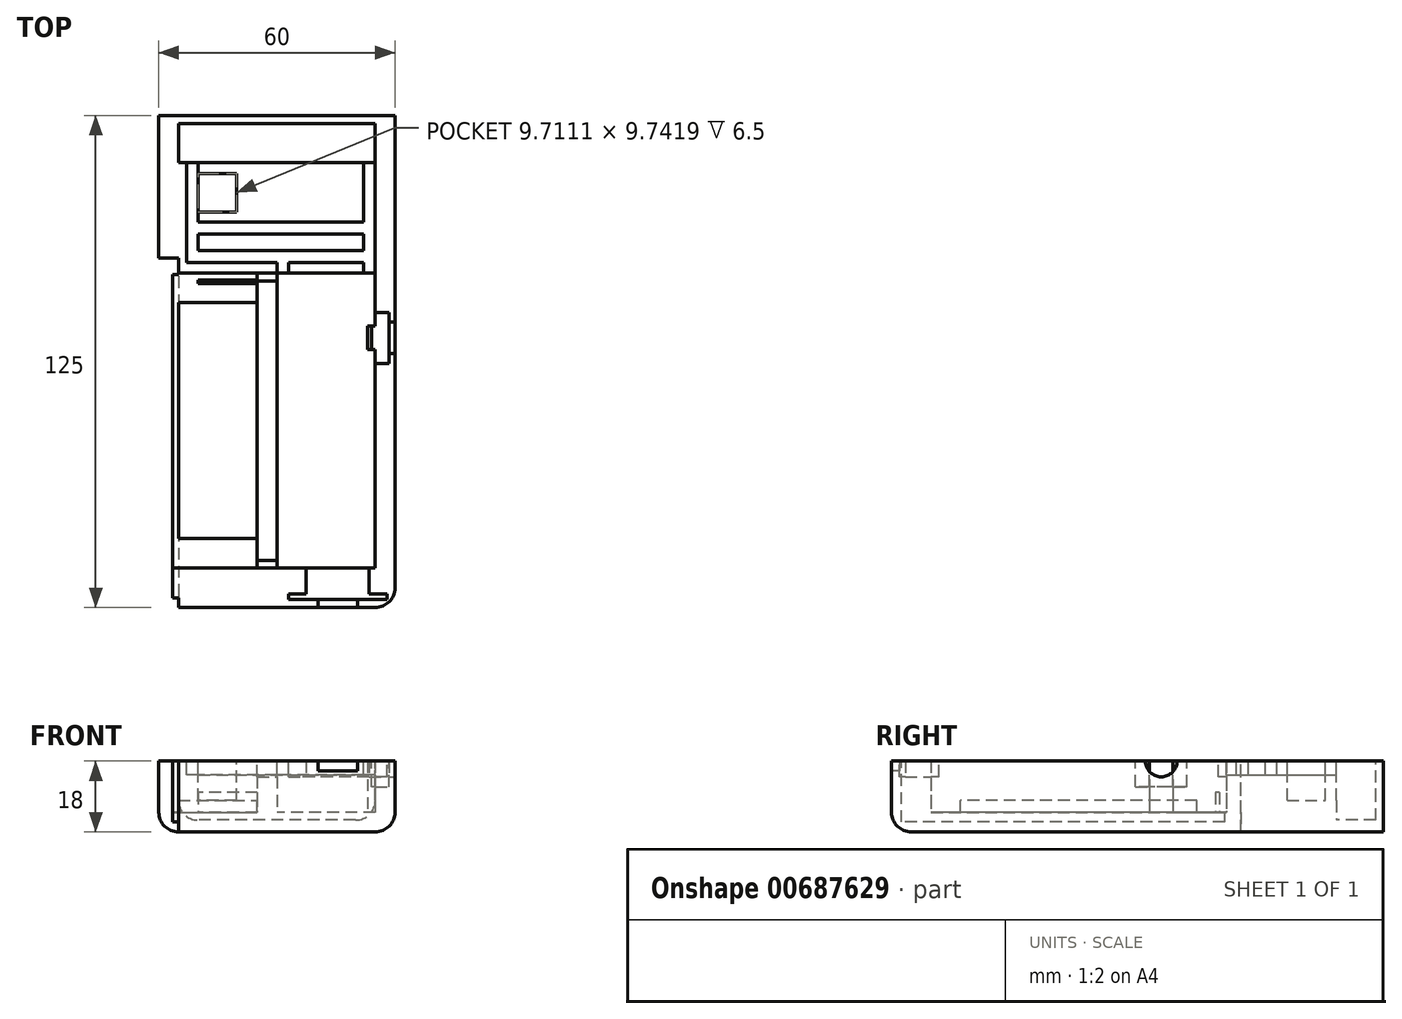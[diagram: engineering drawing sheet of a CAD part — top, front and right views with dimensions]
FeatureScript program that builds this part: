
annotation { "Feature Type Name" : "Feature", "Feature Type Description" : "" }
export const myFeature = defineFeature(function(context is Context, id is Id, definition is map)
    precondition{}
    {
        {
            var Q0;
            Q0=qCreatedBy(makeId("Top.planeOp"),FACE);
            var sketch = newSketch(context, id + "F0", { "sketchPlane" : qUnion([Q0])});
            skLineSegment(sketch, "E0.bottom", {"start": v(-46.34, 47.02) * mm, "end": v(13.66, 47.02) * mm});
            skLineSegment(sketch, "E0.top", {"start": v(-46.34, -52.98) * mm, "end": v(13.66, -52.98) * mm});
            skLineSegment(sketch, "E0.left", {"start": v(-46.34, 47.02) * mm, "end": v(-46.34, -52.98) * mm});
            skLineSegment(sketch, "E0.right", {"start": v(13.66, 47.02) * mm, "end": v(13.66, -52.98) * mm});
            skLineSegment(sketch, "E1.bottom", {"start": v(8.66, -42.98) * mm, "end": v(-16.34, -42.98) * mm});
            skLineSegment(sketch, "E1.top", {"start": v(8.66, 32.02) * mm, "end": v(-16.34, 32.02) * mm});
            skLineSegment(sketch, "E1.left", {"start": v(8.66, -42.98) * mm, "end": v(8.66, 32.02) * mm});
            skLineSegment(sketch, "E1.right", {"start": v(-16.34, -42.98) * mm, "end": v(-16.34, 32.02) * mm});
            skLineSegment(sketch, "E2.bottom", {"start": v(-41.34, 32.02) * mm, "end": v(-21.34, 32.02) * mm});
            skLineSegment(sketch, "E2.top", {"start": v(-41.34, -42.98) * mm, "end": v(-21.34, -42.98) * mm});
            skLineSegment(sketch, "E2.left", {"start": v(-41.34, 32.02) * mm, "end": v(-41.34, -42.98) * mm});
            skLineSegment(sketch, "E2.right", {"start": v(-21.34, 32.02) * mm, "end": v(-21.34, -42.98) * mm});
            skLineSegment(sketch, "E3.bottom", {"start": v(-46.34, 47.02) * mm, "end": v(-26.34, 47.02) * mm});
            skLineSegment(sketch, "E4.bottom", {"start": v(13.66, 47.02) * mm, "end": v(-6.34, 47.02) * mm});
            skSolve(sketch);
        }
        {
            var Q0;
            Q0=makeQuery(id+"F0.imprint","IMPRINT",FACE,{"disambiguationData":[TD([[makeQuery(id+"F0.imprint","IMPRINT",EDGE,{"derivedFrom":sQuery(id+"F0.wireOp",EDGE,"E0.bottom")}),-1.0]])]});
            extrude(context, id + "F1", {"entities" : qUnion([Q0]), "depth" : 13 * mm, "offsetDistance" : 25 * mm});
        }
        {
            var Q0;
            Q0=makeQuery(id+"F0.imprint","IMPRINT",FACE,{"disambiguationData":[TD([[makeQuery(id+"F0.imprint","IMPRINT",EDGE,{"derivedFrom":sQuery(id+"F0.wireOp",EDGE,"E1.bottom")}),-1.0]])]});
            var Q1;
            Q1=makeQuery(id+"F0.imprint","IMPRINT",FACE,{"disambiguationData":[TD([[makeQuery(id+"F0.imprint","IMPRINT",EDGE,{"derivedFrom":sQuery(id+"F0.wireOp",EDGE,"E2.bottom")}),-1.0]])]});
            var Q2;
            Q2=makeQuery(id+"F0.imprint","IMPRINT",FACE,{"disambiguationData":[TD([[makeQuery(id+"F0.imprint","IMPRINT",EDGE,{"derivedFrom":sQuery(id+"F0.wireOp",EDGE,"E0.bottom")}),-1.0]])]});
            extrude(context, id + "F2", {"entities" : qUnion([Q0, Q1, Q2]), "operationType" : NewBodyOperationType.ADD, "oppositeDirection" : true, "depth" : 5 * mm, "offsetDistance" : 25 * mm});
        }
        {
            var Q0;
            {var subQ0=sQuery(id+"F0.wireOp",EDGE,"E0.right");Q0=makeQuery(id+"F2.boolean.opBoolean","MERGE",FACE,{"derivedFrom":[makeQuery(id+"F1.opExtrude","SWEPT_FACE",FACE,{"disambiguationData":[OSD([subQ0])]}),makeQuery(id+"F2.opExtrude","SWEPT_FACE",FACE,{"disambiguationData":[OSD([subQ0])]})]});}
            var sketch = newSketch(context, id + "F3", { "sketchPlane" : qUnion([Q0])});
            skCircle(sketch, "E5", {"center": v(15.53, 13) * mm, "radius": 4 * mm});
            skSolve(sketch);
        }
        {
            var Q0;
            Q0 = qSketchRegion(id + "F3", true);
            extrude(context, id + "F4", {"entities" : qUnion([Q0]), "operationType" : NewBodyOperationType.REMOVE, "oppositeDirection" : true, "depth" : 5 * mm, "offsetDistance" : 25 * mm});
        }
        {
            var Q0;
            {var subQ0=sQuery(id+"F0.wireOp",EDGE,"E4.bottom");var subQ1=sQuery(id+"F0.wireOp",EDGE,"E3.bottom");Q0=makeQuery(id+"FooMiOLfBCFiUER_0.boolean.opBoolean","MERGE",FACE,{"derivedFrom":[makeQuery(id+"F1.opExtrude","CAP_FACE",FACE,{"disambiguationData":[OSD([sQuery(id+"F0.wireOp",EDGE,"E0.bottom"),sQuery(id+"F0.wireOp",EDGE,"E0.top"),sQuery(id+"F0.wireOp",EDGE,"E0.left"),sQuery(id+"F0.wireOp",EDGE,"E0.right"),sQuery(id+"F0.wireOp",EDGE,"E1.bottom"),sQuery(id+"F0.wireOp",EDGE,"E1.top"),sQuery(id+"F0.wireOp",EDGE,"E1.left"),sQuery(id+"F0.wireOp",EDGE,"E1.right"),sQuery(id+"F0.wireOp",EDGE,"E2.bottom"),sQuery(id+"F0.wireOp",EDGE,"E2.top"),sQuery(id+"F0.wireOp",EDGE,"E2.left"),sQuery(id+"F0.wireOp",EDGE,"E2.right"),subQ1,subQ0])],"isStart":false}),makeQuery(id+"FooMiOLfBCFiUER_0.opExtrude","CAP_FACE",FACE,{"disambiguationData":[OSD([subQ1,sQuery(id+"F0.wireOp",EDGE,"E3.top"),sQuery(id+"F0.wireOp",EDGE,"E3.right"),sQuery(id+"F0.wireOp",EDGE,"7eb4718d-a1aa-4163-babb-219306aed6bf")])],"isStart":false}),makeQuery(id+"FooMiOLfBCFiUER_0.opExtrude","CAP_FACE",FACE,{"disambiguationData":[OSD([subQ0,sQuery(id+"F0.wireOp",EDGE,"E4.top"),sQuery(id+"F0.wireOp",EDGE,"E4.right"),sQuery(id+"F0.wireOp",EDGE,"1b457c1d-76ec-41e5-a347-412c3d054c09")])],"isStart":false})]});}
            var sketch = newSketch(context, id + "F5", { "sketchPlane" : qUnion([Q0])});
            skLineSegment(sketch, "E6.bottom", {"start": v(8.66, 22.03) * mm, "end": v(12.16, 22.03) * mm});
            skLineSegment(sketch, "E6.top", {"start": v(8.66, 9.03) * mm, "end": v(12.16, 9.03) * mm});
            skLineSegment(sketch, "E6.left", {"start": v(8.66, 22.03) * mm, "end": v(8.66, 9.03) * mm});
            skLineSegment(sketch, "E6.right", {"start": v(12.16, 22.03) * mm, "end": v(12.16, 9.03) * mm});
            skSolve(sketch);
        }
        {
            var Q0;
            Q0 = qSketchRegion(id + "F5", true);
            extrude(context, id + "F6", {"entities" : qUnion([Q0]), "operationType" : NewBodyOperationType.REMOVE, "oppositeDirection" : true, "depth" : 6.5 * mm, "offsetDistance" : 25 * mm});
        }
        {
            var Q0;
            {var subQ0=sQuery(id+"F0.wireOp",EDGE,"E0.left");Q0=makeQuery(id+"F2.boolean.opBoolean","MERGE",FACE,{"derivedFrom":[makeQuery(id+"F1.opExtrude","SWEPT_FACE",FACE,{"disambiguationData":[OSD([subQ0])]}),makeQuery(id+"F2.opExtrude","SWEPT_FACE",FACE,{"disambiguationData":[OSD([subQ0])]})]});}
            var sketch = newSketch(context, id + "F7", { "sketchPlane" : qUnion([Q0])});
            skLineSegment(sketch, "E7.bottom", {"start": v(-35.8, -5) * mm, "end": v(52.98, -5) * mm});
            skLineSegment(sketch, "E7.top", {"start": v(-35.8, 13) * mm, "end": v(52.98, 13) * mm});
            skLineSegment(sketch, "E7.left", {"start": v(-35.8, -5) * mm, "end": v(-35.8, 13) * mm});
            skLineSegment(sketch, "E7.right", {"start": v(52.98, -5) * mm, "end": v(52.98, 13) * mm});
            skSolve(sketch);
        }
        {
            var Q0;
            Q0 = qSketchRegion(id + "F7", true);
            extrude(context, id + "F8", {"entities" : qUnion([Q0]), "operationType" : NewBodyOperationType.REMOVE, "oppositeDirection" : true, "depth" : 5 * mm, "offsetDistance" : 25 * mm});
        }
        {
            var Q0;
            Q0=makeQuery(id+"F8.boolean.opBoolean","COPY",FACE,{"derivedFrom":makeQuery(id+"F8.opExtrude","CAP_FACE",FACE,{"disambiguationData":[OSD([sQuery(id+"F7.wireOp",EDGE,"E7.bottom"),sQuery(id+"F7.wireOp",EDGE,"E7.top"),sQuery(id+"F7.wireOp",EDGE,"E7.left"),sQuery(id+"F7.wireOp",EDGE,"E7.right")])],"isStart":false})});
            var sketch = newSketch(context, id + "F9", { "sketchPlane" : qUnion([Q0])});
            skLineSegment(sketch, "E8.bottom", {"start": v(-33.3, -2.5) * mm, "end": v(50.48, -2.5) * mm});
            skLineSegment(sketch, "E8.top", {"start": v(-33.3, 13) * mm, "end": v(50.48, 13) * mm});
            skLineSegment(sketch, "E8.left", {"start": v(-33.3, -2.5) * mm, "end": v(-33.3, 13) * mm});
            skLineSegment(sketch, "E8.right", {"start": v(50.48, -2.5) * mm, "end": v(50.48, 13) * mm});
            skSolve(sketch);
        }
        {
            var Q0;
            Q0=makeQuery(id+"F9.imprint","IMPRINT",FACE,{"disambiguationData":[TD([[makeQuery(id+"F9.imprint","IMPRINT",EDGE,{"derivedFrom":sQuery(id+"F9.wireOp",EDGE,"E8.bottom")}),1.0]])]});
            extrude(context, id + "F10", {"entities" : qUnion([Q0]), "operationType" : NewBodyOperationType.ADD, "depth" : 5 * mm, "offsetDistance" : 25 * mm});
        }
        {
            var Q0;
            Q0=makeQuery(id+"F10.opExtrude","CAP_FACE",FACE,{"disambiguationData":[OSD([sQuery(id+"F0.wireOp",EDGE,"E2.bottom"),sQuery(id+"F0.wireOp",EDGE,"E2.top"),sQuery(id+"F0.wireOp",EDGE,"E2.left"),sQuery(id+"F9.wireOp",EDGE,"E8.bottom"),sQuery(id+"F9.wireOp",EDGE,"E8.top"),sQuery(id+"F9.wireOp",EDGE,"E8.left"),sQuery(id+"F9.wireOp",EDGE,"E8.right")])],"isStart":false});
            var sketch = newSketch(context, id + "F11", { "sketchPlane" : qUnion([Q0])});
            skLineSegment(sketch, "E9.bottom", {"start": v(-33.3, 13) * mm, "end": v(-32.02, 13) * mm});
            skLineSegment(sketch, "E9.top", {"start": v(-33.3, 0) * mm, "end": v(-32.02, 0) * mm});
            skLineSegment(sketch, "E9.left", {"start": v(-33.3, 13) * mm, "end": v(-33.3, 0) * mm});
            skLineSegment(sketch, "E9.right", {"start": v(-32.02, 13) * mm, "end": v(-32.02, 0) * mm});
            skSolve(sketch);
        }
        {
            var Q0;
            Q0 = qSketchRegion(id + "F11", true);
            extrude(context, id + "F12", {"entities" : qUnion([Q0]), "operationType" : NewBodyOperationType.REMOVE, "oppositeDirection" : true, "depth" : 5 * mm, "offsetDistance" : 25 * mm});
        }
        {
            var Q0;
            {var subQ0=sQuery(id+"F9.wireOp",EDGE,"E8.top");var subQ1=sQuery(id+"F0.wireOp",EDGE,"E2.left");var subQ2=sQuery(id+"F0.wireOp",EDGE,"E2.top");var subQ3=sQuery(id+"F0.wireOp",EDGE,"E0.top");var subQ4=sQuery(id+"F0.wireOp",EDGE,"E3.bottom");var subQ5=makeQuery(id+"FooMiOLfBCFiUER_0.opExtrude","CAP_FACE",FACE,{"disambiguationData":[OSD([subQ4,sQuery(id+"F0.wireOp",EDGE,"E3.top"),sQuery(id+"F0.wireOp",EDGE,"E3.right"),sQuery(id+"F0.wireOp",EDGE,"7eb4718d-a1aa-4163-babb-219306aed6bf")])],"isStart":false});var subQ6=sQuery(id+"F0.wireOp",EDGE,"E4.bottom");var subQ7=sQuery(id+"F0.wireOp",EDGE,"E2.bottom");var subQ8=makeQuery(id+"F1.opExtrude","CAP_FACE",FACE,{"disambiguationData":[OSD([sQuery(id+"F0.wireOp",EDGE,"E0.bottom"),subQ3,sQuery(id+"F0.wireOp",EDGE,"E0.left"),sQuery(id+"F0.wireOp",EDGE,"E0.right"),sQuery(id+"F0.wireOp",EDGE,"E1.bottom"),sQuery(id+"F0.wireOp",EDGE,"E1.top"),sQuery(id+"F0.wireOp",EDGE,"E1.left"),sQuery(id+"F0.wireOp",EDGE,"E1.right"),subQ7,subQ2,subQ1,sQuery(id+"F0.wireOp",EDGE,"E2.right"),subQ4,subQ6])],"isStart":false});var subQ12=makeQuery(id+"FooMiOLfBCFiUER_0.opExtrude","CAP_FACE",FACE,{"disambiguationData":[OSD([subQ6,sQuery(id+"F0.wireOp",EDGE,"E4.top"),sQuery(id+"F0.wireOp",EDGE,"E4.right"),sQuery(id+"F0.wireOp",EDGE,"1b457c1d-76ec-41e5-a347-412c3d054c09")])],"isStart":false});Q0=makeQuery(id+"F10.boolean.opBoolean","MERGE",FACE,{"derivedFrom":[makeQuery(id+"FooMiOLfBCFiUER_0.boolean.opBoolean","MERGE",FACE,{"derivedFrom":[subQ8,subQ5,subQ12]}),makeQuery(id+"F10.opExtrude","SWEPT_FACE",FACE,{"disambiguationData":[OSD([subQ0]),TDD([makeQuery(id+"F9.imprint","IMPRINT",EDGE,{"disambiguationData":[TD([[makeQuery(id+"F9.imprint","INTERSECT",VERTEX,{"derivedFrom":[makeQuery(id+"F1.opExtrude","SWEPT_EDGE",EDGE,{"disambiguationData":[OSD([subQ7,subQ1])]}),subQ0]}),1.0]])],"derivedFrom":subQ0})])]}),makeQuery(id+"F10.opExtrude","SWEPT_FACE",FACE,{"disambiguationData":[OSD([subQ0]),TDD([makeQuery(id+"F9.imprint","IMPRINT",EDGE,{"disambiguationData":[TD([[makeQuery(id+"F9.imprint","INTERSECT",VERTEX,{"derivedFrom":[makeQuery(id+"F1.opExtrude","SWEPT_EDGE",EDGE,{"disambiguationData":[OSD([subQ2,subQ1])]}),subQ0]}),-1.0]])],"derivedFrom":subQ0})])]})]});}
            var sketch = newSketch(context, id + "F13", { "sketchPlane" : qUnion([Q0])});
            skPoint(sketch, "E10.oppositeSnap0", {"position": v(5.66, 43.01) * mm});
            skLineSegment(sketch, "E10.bottom", {"start": v(8.66, 32.02) * mm, "end": v(5.66, 32.02) * mm});
            skLineSegment(sketch, "E10.top", {"start": v(8.66, 42.02) * mm, "end": v(5.66, 42.02) * mm});
            skLineSegment(sketch, "E10.left", {"start": v(8.66, 32.02) * mm, "end": v(8.66, 42.02) * mm});
            skLineSegment(sketch, "E10.right", {"start": v(5.66, 32.02) * mm, "end": v(5.66, 42.02) * mm});
            skLineSegment(sketch, "E11.bottom", {"start": v(5.66, 34.7) * mm, "end": v(-37.04, 34.7) * mm});
            skLineSegment(sketch, "E11.top", {"start": v(5.66, 37.7) * mm, "end": v(-37.04, 37.7) * mm});
            skLineSegment(sketch, "E11.left", {"start": v(5.66, 34.7) * mm, "end": v(5.66, 37.7) * mm});
            skLineSegment(sketch, "E11.right", {"start": v(-37.04, 34.7) * mm, "end": v(-37.04, 37.7) * mm});
            skLineSegment(sketch, "E12.bottom", {"start": v(-36.29, 34.7) * mm, "end": v(-39.29, 34.7) * mm});
            skLineSegment(sketch, "E12.top", {"start": v(-36.29, 41.96) * mm, "end": v(-39.29, 41.96) * mm});
            skLineSegment(sketch, "E12.left", {"start": v(-36.29, 34.7) * mm, "end": v(-36.29, 41.96) * mm});
            skLineSegment(sketch, "E12.right", {"start": v(-39.29, 34.7) * mm, "end": v(-39.29, 41.96) * mm});
            skLineSegment(sketch, "E13.bottom", {"start": v(-16.34, 32.02) * mm, "end": v(-13.34, 32.02) * mm});
            skLineSegment(sketch, "E13.top", {"start": v(-16.34, 35.93) * mm, "end": v(-13.34, 35.93) * mm});
            skLineSegment(sketch, "E13.left", {"start": v(-16.34, 32.02) * mm, "end": v(-16.34, 35.93) * mm});
            skLineSegment(sketch, "E13.right", {"start": v(-13.34, 32.02) * mm, "end": v(-13.34, 35.93) * mm});
            skSolve(sketch);
        }
        {
            var Q0;
            Q0 = qSketchRegion(id + "F13", true);
            extrude(context, id + "F14", {"entities" : qUnion([Q0]), "operationType" : NewBodyOperationType.REMOVE, "oppositeDirection" : true, "depth" : 3.5 * mm, "offsetDistance" : 25 * mm});
        }
        {
            var Q0;
            {var subQ2=sQuery(id+"F9.wireOp",EDGE,"E8.top");var subQ3=sQuery(id+"F0.wireOp",EDGE,"E2.left");var subQ4=sQuery(id+"F0.wireOp",EDGE,"E2.top");var subQ5=sQuery(id+"F0.wireOp",EDGE,"E2.bottom");var subQ6=sQuery(id+"F0.wireOp",EDGE,"E2.right");var subQ9=sQuery(id+"F0.wireOp",EDGE,"E3.top");var subQ12=sQuery(id+"F0.wireOp",EDGE,"E0.right");var subQ13=sQuery(id+"F0.wireOp",EDGE,"7eb4718d-a1aa-4163-babb-219306aed6bf");var subQ14=sQuery(id+"F0.wireOp",EDGE,"E1.bottom");var subQ15=sQuery(id+"F0.wireOp",EDGE,"E0.left");var subQ16=sQuery(id+"F0.wireOp",EDGE,"E0.top");var subQ17=makeQuery(id+"F1.opExtrude","SWEPT_FACE",FACE,{"disambiguationData":[OSD([subQ16])]});var subQ18=sQuery(id+"F0.wireOp",EDGE,"E1.left");var subQ19=sQuery(id+"F0.wireOp",EDGE,"E1.right");var subQ23=sQuery(id+"F0.wireOp",EDGE,"E3.bottom");var subQ24=makeQuery(id+"FooMiOLfBCFiUER_0.opExtrude","CAP_FACE",FACE,{"disambiguationData":[OSD([subQ23,subQ9,sQuery(id+"F0.wireOp",EDGE,"E3.right"),subQ13])],"isStart":false});var subQ25=sQuery(id+"F0.wireOp",EDGE,"E4.bottom");var subQ26=makeQuery(id+"F1.opExtrude","CAP_FACE",FACE,{"disambiguationData":[OSD([sQuery(id+"F0.wireOp",EDGE,"E0.bottom"),subQ16,subQ15,subQ12,subQ14,sQuery(id+"F0.wireOp",EDGE,"E1.top"),subQ18,subQ19,subQ5,subQ4,subQ3,subQ6,subQ23,subQ25])],"isStart":false});var subQ27=makeQuery(id+"FooMiOLfBCFiUER_0.opExtrude","CAP_FACE",FACE,{"disambiguationData":[OSD([subQ25,sQuery(id+"F0.wireOp",EDGE,"E4.top"),sQuery(id+"F0.wireOp",EDGE,"E4.right"),sQuery(id+"F0.wireOp",EDGE,"1b457c1d-76ec-41e5-a347-412c3d054c09")])],"isStart":false});Q0=makeQuery(id+"F14.boolean.opBoolean","SPLIT",FACE,{"disambiguationData":[TD([subQ17])],"derivedFrom":makeQuery(id+"F10.boolean.opBoolean","MERGE",FACE,{"derivedFrom":[makeQuery(id+"FooMiOLfBCFiUER_0.boolean.opBoolean","MERGE",FACE,{"derivedFrom":[subQ26,subQ24,subQ27]}),makeQuery(id+"F10.opExtrude","SWEPT_FACE",FACE,{"disambiguationData":[OSD([subQ2]),TDD([makeQuery(id+"F9.imprint","IMPRINT",EDGE,{"disambiguationData":[TD([[makeQuery(id+"F9.imprint","INTERSECT",VERTEX,{"derivedFrom":[makeQuery(id+"F1.opExtrude","SWEPT_EDGE",EDGE,{"disambiguationData":[OSD([subQ5,subQ3])]}),subQ2]}),1.0]])],"derivedFrom":subQ2})])]}),makeQuery(id+"F10.opExtrude","SWEPT_FACE",FACE,{"disambiguationData":[OSD([subQ2]),TDD([makeQuery(id+"F9.imprint","IMPRINT",EDGE,{"disambiguationData":[TD([[makeQuery(id+"F9.imprint","INTERSECT",VERTEX,{"derivedFrom":[makeQuery(id+"F1.opExtrude","SWEPT_EDGE",EDGE,{"disambiguationData":[OSD([subQ4,subQ3])]}),subQ2]}),-1.0]])],"derivedFrom":subQ2})])]})]})});}
            var sketch = newSketch(context, id + "F15", { "sketchPlane" : qUnion([Q0])});
            skLineSegment(sketch, "E14.bottom", {"start": v(-21.34, 32.02) * mm, "end": v(-16.34, 32.02) * mm});
            skLineSegment(sketch, "E14.top", {"start": v(-21.34, 30.02) * mm, "end": v(-16.34, 30.02) * mm});
            skLineSegment(sketch, "E14.left", {"start": v(-21.34, 32.02) * mm, "end": v(-21.34, 30.02) * mm});
            skLineSegment(sketch, "E14.right", {"start": v(-16.34, 32.02) * mm, "end": v(-16.34, 30.02) * mm});
            skLineSegment(sketch, "E15.bottom", {"start": v(-21.34, -42.98) * mm, "end": v(-16.34, -42.98) * mm});
            skLineSegment(sketch, "E15.top", {"start": v(-21.34, -40.98) * mm, "end": v(-16.34, -40.98) * mm});
            skLineSegment(sketch, "E15.left", {"start": v(-21.34, -42.98) * mm, "end": v(-21.34, -40.98) * mm});
            skLineSegment(sketch, "E15.right", {"start": v(-16.34, -42.98) * mm, "end": v(-16.34, -40.98) * mm});
            skSolve(sketch);
        }
        {
            var Q0;
            Q0 = qSketchRegion(id + "F15", true);
            extrude(context, id + "F16", {"entities" : qUnion([Q0]), "operationType" : NewBodyOperationType.REMOVE, "oppositeDirection" : true, "depth" : 4 * mm, "offsetDistance" : 25 * mm});
        }
        {
            var Q0;
            {var subQ0=sQuery(id+"F0.wireOp",EDGE,"E2.left");Q0=makeQuery(id+"F12.boolean.opBoolean","MERGE",FACE,{"derivedFrom":[makeQuery(id+"F10.boolean.opBoolean","MERGE",FACE,{"derivedFrom":[makeQuery(id+"F2.boolean.opBoolean","SPLIT",FACE,{"disambiguationData":[TD([makeQuery(id+"F1.opExtrude","SWEPT_FACE",FACE,{"disambiguationData":[OSD([sQuery(id+"F0.wireOp",EDGE,"E2.bottom")])]})])],"derivedFrom":makeQuery(id+"F2.opExtrude","CAP_FACE",FACE,{"disambiguationData":[OSD([sQuery(id+"F0.wireOp",EDGE,"E0.bottom"),sQuery(id+"F0.wireOp",EDGE,"E0.top"),sQuery(id+"F0.wireOp",EDGE,"E0.left"),sQuery(id+"F0.wireOp",EDGE,"E0.right"),sQuery(id+"F0.wireOp",EDGE,"E3.bottom"),sQuery(id+"F0.wireOp",EDGE,"E4.bottom")])],"isStart":true})}),makeQuery(id+"F10.opExtrude","SWEPT_FACE",FACE,{"disambiguationData":[OSD([subQ0])]})]}),makeQuery(id+"F12.opExtrude","SWEPT_FACE",FACE,{"disambiguationData":[OSD([sQuery(id+"F11.wireOp",EDGE,"E9.top")])]})]});}
            var sketch = newSketch(context, id + "F17", { "sketchPlane" : qUnion([Q0])});
            skLineSegment(sketch, "E16.bottom", {"start": v(-21.34, 30.29) * mm, "end": v(-36.34, 30.29) * mm});
            skLineSegment(sketch, "E16.top", {"start": v(-21.34, 29.29) * mm, "end": v(-36.34, 29.29) * mm});
            skLineSegment(sketch, "E16.left", {"start": v(-21.34, 30.29) * mm, "end": v(-21.34, 29.29) * mm});
            skLineSegment(sketch, "E16.right", {"start": v(-36.34, 30.29) * mm, "end": v(-36.34, 29.29) * mm});
            skSolve(sketch);
        }
        {
            var Q0;
            Q0 = qSketchRegion(id + "F17", true);
            extrude(context, id + "F18", {"entities" : qUnion([Q0]), "operationType" : NewBodyOperationType.ADD, "depth" : 5 * mm, "offsetDistance" : 25 * mm});
        }
        {
            var Q0;
            Q0=makeQuery(id+"F2.opExtrude","CAP_EDGE",EDGE,{"disambiguationData":[OSD([sQuery(id+"F0.wireOp",EDGE,"E0.right")])],"isStart":false});
            var Q1;
            Q1=makeQuery(id+"F2.opExtrude","CAP_EDGE",EDGE,{"disambiguationData":[OSD([sQuery(id+"F0.wireOp",EDGE,"E0.top")])],"isStart":false});
            var Q2;
            {var subQ0=sQuery(id+"F0.wireOp",EDGE,"E0.right");var subQ1=sQuery(id+"F0.wireOp",EDGE,"E0.top");Q2=makeQuery(id+"F2.boolean.opBoolean","MERGE",EDGE,{"derivedFrom":[makeQuery(id+"F1.opExtrude","SWEPT_EDGE",EDGE,{"disambiguationData":[OSD([subQ1,subQ0])]}),makeQuery(id+"F2.opExtrude","SWEPT_EDGE",EDGE,{"disambiguationData":[OSD([subQ1,subQ0])]})]});}
            var Q3;
            Q3=makeQuery(id+"F2.opExtrude","CAP_EDGE",EDGE,{"disambiguationData":[OSD([sQuery(id+"F0.wireOp",EDGE,"E0.left")])],"isStart":false});
            fillet(context, id + "F19", {"entities" : qUnion([Q0, Q1, Q2, Q3]), "radius" : 5 * mm, "tangentPropagation" : true, "allowEdgeOverflow" : false});
        }
        {
            var Q0;
            {var subQ0=sQuery(id+"F0.wireOp",EDGE,"E0.top");Q0=makeQuery(id+"F2.boolean.opBoolean","MERGE",FACE,{"derivedFrom":[makeQuery(id+"F1.opExtrude","SWEPT_FACE",FACE,{"disambiguationData":[OSD([subQ0])]}),makeQuery(id+"F2.opExtrude","SWEPT_FACE",FACE,{"disambiguationData":[OSD([subQ0])]})]});}
            var sketch = newSketch(context, id + "F20", { "sketchPlane" : qUnion([Q0])});
            skLineSegment(sketch, "E17.bottom", {"start": v(4.12, 13) * mm, "end": v(-5.88, 13) * mm});
            skLineSegment(sketch, "E17.top", {"start": v(4.12, 10.5) * mm, "end": v(-5.88, 10.5) * mm});
            skLineSegment(sketch, "E17.left", {"start": v(4.12, 13) * mm, "end": v(4.12, 10.5) * mm});
            skLineSegment(sketch, "E17.right", {"start": v(-5.88, 13) * mm, "end": v(-5.88, 10.5) * mm});
            skSolve(sketch);
        }
        {
            var Q0;
            Q0 = qSketchRegion(id + "F20", true);
            extrude(context, id + "F21", {"entities" : qUnion([Q0]), "operationType" : NewBodyOperationType.REMOVE, "oppositeDirection" : true, "depth" : 10 * mm, "offsetDistance" : 25 * mm});
        }
        {
            var Q0;
            {var subQ0=sQuery(id+"F0.wireOp",EDGE,"E2.top");Q0=makeQuery(id+"F16.boolean.opBoolean","MERGE",FACE,{"derivedFrom":[makeQuery(id+"F1.opExtrude","SWEPT_FACE",FACE,{"disambiguationData":[OSD([sQuery(id+"F0.wireOp",EDGE,"E1.bottom")])]}),makeQuery(id+"F10.boolean.opBoolean","MERGE",FACE,{"derivedFrom":[makeQuery(id+"F1.opExtrude","SWEPT_FACE",FACE,{"disambiguationData":[OSD([subQ0])]}),makeQuery(id+"F10.opExtrude","SWEPT_FACE",FACE,{"disambiguationData":[OSD([subQ0,sQuery(id+"F0.wireOp",EDGE,"E2.left")])]})]}),makeQuery(id+"F16.opExtrude","SWEPT_FACE",FACE,{"disambiguationData":[OSD([sQuery(id+"F15.wireOp",EDGE,"E15.bottom")])]})]});}
            var sketch = newSketch(context, id + "F22", { "sketchPlane" : qUnion([Q0])});
            skLineSegment(sketch, "E18.bottom", {"start": v(-7.12, 13) * mm, "end": v(8.88, 13) * mm});
            skLineSegment(sketch, "E18.top", {"start": v(-7.12, 9) * mm, "end": v(8.88, 9) * mm});
            skLineSegment(sketch, "E18.left", {"start": v(-7.12, 13) * mm, "end": v(-7.12, 9) * mm});
            skLineSegment(sketch, "E18.right", {"start": v(8.88, 13) * mm, "end": v(8.88, 9) * mm});
            skSolve(sketch);
        }
        {
            var Q0;
            Q0 = qSketchRegion(id + "F22", true);
            extrude(context, id + "F23", {"entities" : qUnion([Q0]), "operationType" : NewBodyOperationType.REMOVE, "oppositeDirection" : true, "depth" : 8 * mm, "offsetDistance" : 25 * mm});
        }
        {
            var Q0;
            {var subQ2=sQuery(id+"F0.wireOp",EDGE,"E0.right");var subQ4=sQuery(id+"F0.wireOp",EDGE,"E0.top");var subQ8=sQuery(id+"F0.wireOp",EDGE,"E1.left");var subQ10=sQuery(id+"F0.wireOp",EDGE,"E2.left");var subQ11=sQuery(id+"F0.wireOp",EDGE,"E2.top");var subQ14=makeQuery(id+"F1.opExtrude","SWEPT_FACE",FACE,{"disambiguationData":[OSD([subQ4])]});var subQ15=makeQuery(id+"F1.opExtrude","SWEPT_FACE",FACE,{"disambiguationData":[OSD([subQ2])]});var subQ16=sQuery(id+"F0.wireOp",EDGE,"E1.bottom");var subQ26=sQuery(id+"F9.wireOp",EDGE,"E8.top");var subQ27=sQuery(id+"F0.wireOp",EDGE,"E2.bottom");var subQ30=sQuery(id+"F0.wireOp",EDGE,"E2.right");var subQ32=sQuery(id+"F0.wireOp",EDGE,"E3.top");var subQ33=sQuery(id+"F0.wireOp",EDGE,"7eb4718d-a1aa-4163-babb-219306aed6bf");var subQ34=sQuery(id+"F0.wireOp",EDGE,"E0.left");var subQ35=sQuery(id+"F0.wireOp",EDGE,"E1.right");var subQ37=sQuery(id+"F0.wireOp",EDGE,"E3.bottom");var subQ38=makeQuery(id+"FooMiOLfBCFiUER_0.opExtrude","CAP_FACE",FACE,{"disambiguationData":[OSD([subQ37,subQ32,sQuery(id+"F0.wireOp",EDGE,"E3.right"),subQ33])],"isStart":false});var subQ39=sQuery(id+"F0.wireOp",EDGE,"E4.bottom");var subQ40=makeQuery(id+"F1.opExtrude","CAP_FACE",FACE,{"disambiguationData":[OSD([sQuery(id+"F0.wireOp",EDGE,"E0.bottom"),subQ4,subQ34,subQ2,subQ16,sQuery(id+"F0.wireOp",EDGE,"E1.top"),subQ8,subQ35,subQ27,subQ11,subQ10,subQ30,subQ37,subQ39])],"isStart":false});var subQ41=makeQuery(id+"FooMiOLfBCFiUER_0.opExtrude","CAP_FACE",FACE,{"disambiguationData":[OSD([subQ39,sQuery(id+"F0.wireOp",EDGE,"E4.top"),sQuery(id+"F0.wireOp",EDGE,"E4.right"),sQuery(id+"F0.wireOp",EDGE,"1b457c1d-76ec-41e5-a347-412c3d054c09")])],"isStart":false});Q0=makeQuery(id+"F21.boolean.opBoolean","SPLIT",FACE,{"disambiguationData":[TD([subQ15])],"derivedFrom":makeQuery(id+"F16.boolean.opBoolean","SPLIT",FACE,{"disambiguationData":[TD([subQ14])],"derivedFrom":makeQuery(id+"F14.boolean.opBoolean","SPLIT",FACE,{"disambiguationData":[TD([subQ14])],"derivedFrom":makeQuery(id+"F10.boolean.opBoolean","MERGE",FACE,{"derivedFrom":[makeQuery(id+"FooMiOLfBCFiUER_0.boolean.opBoolean","MERGE",FACE,{"derivedFrom":[subQ40,subQ38,subQ41]}),makeQuery(id+"F10.opExtrude","SWEPT_FACE",FACE,{"disambiguationData":[OSD([subQ26]),TDD([makeQuery(id+"F9.imprint","IMPRINT",EDGE,{"disambiguationData":[TD([[makeQuery(id+"F9.imprint","INTERSECT",VERTEX,{"derivedFrom":[makeQuery(id+"F1.opExtrude","SWEPT_EDGE",EDGE,{"disambiguationData":[OSD([subQ27,subQ10])]}),subQ26]}),1.0]])],"derivedFrom":subQ26})])]}),makeQuery(id+"F10.opExtrude","SWEPT_FACE",FACE,{"disambiguationData":[OSD([subQ26]),TDD([makeQuery(id+"F9.imprint","IMPRINT",EDGE,{"disambiguationData":[TD([[makeQuery(id+"F9.imprint","INTERSECT",VERTEX,{"derivedFrom":[makeQuery(id+"F1.opExtrude","SWEPT_EDGE",EDGE,{"disambiguationData":[OSD([subQ11,subQ10])]}),subQ26]}),-1.0]])],"derivedFrom":subQ26})])]})]})})})});}
            var sketch = newSketch(context, id + "F24", { "sketchPlane" : qUnion([Q0])});
            skLineSegment(sketch, "E19.bottom", {"start": v(-13.38, -49.48) * mm, "end": v(11.62, -49.48) * mm});
            skLineSegment(sketch, "E19.top", {"start": v(-13.38, -50.98) * mm, "end": v(11.62, -50.98) * mm});
            skLineSegment(sketch, "E19.left", {"start": v(-13.38, -49.48) * mm, "end": v(-13.38, -50.98) * mm});
            skLineSegment(sketch, "E19.right", {"start": v(11.62, -49.48) * mm, "end": v(11.62, -50.98) * mm});
            skSolve(sketch);
        }
        {
            var Q0;
            Q0 = qSketchRegion(id + "F24", true);
            extrude(context, id + "F25", {"entities" : qUnion([Q0]), "operationType" : NewBodyOperationType.REMOVE, "oppositeDirection" : true, "depth" : 4 * mm, "offsetDistance" : 25 * mm});
        }
        {
            var Q0;
            Q0=makeQuery(id+"F10.opExtrude","CAP_FACE",FACE,{"disambiguationData":[OSD([sQuery(id+"F0.wireOp",EDGE,"E2.bottom"),sQuery(id+"F0.wireOp",EDGE,"E2.top"),sQuery(id+"F0.wireOp",EDGE,"E2.left"),sQuery(id+"F9.wireOp",EDGE,"E8.bottom"),sQuery(id+"F9.wireOp",EDGE,"E8.top"),sQuery(id+"F9.wireOp",EDGE,"E8.left"),sQuery(id+"F9.wireOp",EDGE,"E8.right")])],"isStart":false});
            var sketch = newSketch(context, id + "F26", { "sketchPlane" : qUnion([Q0])});
            skLineSegment(sketch, "E20", {"start": v(-33.3, -2.5) * mm, "end": v(50.48, -2.5) * mm});
            skLineSegment(sketch, "E21", {"start": v(50.48, -2.5) * mm, "end": v(50.48, 13) * mm});
            skLineSegment(sketch, "E22", {"start": v(50.48, 13) * mm, "end": v(42.98, 13) * mm});
            skLineSegment(sketch, "E23", {"start": v(42.98, 13) * mm, "end": v(42.98, 0) * mm});
            skLineSegment(sketch, "E24", {"start": v(42.98, 0) * mm, "end": v(-33.3, 0) * mm});
            skLineSegment(sketch, "E25", {"start": v(-33.3, 0) * mm, "end": v(-33.3, -2.5) * mm});
            skSolve(sketch);
        }
        {
            var Q0;
            Q0 = qSketchRegion(id + "F26", true);
            extrude(context, id + "F27", {"entities" : qUnion([Q0]), "operationType" : NewBodyOperationType.REMOVE, "oppositeDirection" : true, "depth" : 3.5 * mm, "offsetDistance" : 25 * mm});
        }
        {
            var Q0;
            Q0=makeQuery(id+"F2.boolean.opBoolean","SPLIT",FACE,{"disambiguationData":[TD([makeQuery(id+"F1.opExtrude","SWEPT_FACE",FACE,{"disambiguationData":[OSD([sQuery(id+"F0.wireOp",EDGE,"E1.bottom")])]})])],"derivedFrom":makeQuery(id+"F2.opExtrude","CAP_FACE",FACE,{"disambiguationData":[OSD([sQuery(id+"F0.wireOp",EDGE,"E0.bottom"),sQuery(id+"F0.wireOp",EDGE,"E0.top"),sQuery(id+"F0.wireOp",EDGE,"E0.left"),sQuery(id+"F0.wireOp",EDGE,"E0.right"),sQuery(id+"F0.wireOp",EDGE,"E3.bottom"),sQuery(id+"F0.wireOp",EDGE,"E4.bottom")])],"isStart":true})});
            var sketch = newSketch(context, id + "F28", { "sketchPlane" : qUnion([Q0])});
            skLineSegment(sketch, "E26.bottom", {"start": v(8.66, 18.53) * mm, "end": v(6.66, 18.53) * mm});
            skLineSegment(sketch, "E26.top", {"start": v(8.66, 12.53) * mm, "end": v(6.66, 12.53) * mm});
            skLineSegment(sketch, "E26.left", {"start": v(8.66, 18.53) * mm, "end": v(8.66, 12.53) * mm});
            skLineSegment(sketch, "E26.right", {"start": v(6.66, 18.53) * mm, "end": v(6.66, 12.53) * mm});
            skSolve(sketch);
        }
        {
            var Q0;
            Q0=makeQuery(id+"F28.imprint","IMPRINT",FACE,{"disambiguationData":[TD([[makeQuery(id+"F28.imprint","IMPRINT",EDGE,{"derivedFrom":sQuery(id+"F28.wireOp",EDGE,"E26.bottom")}),1.0]])]});
            extrude(context, id + "F29", {"entities" : qUnion([Q0]), "operationType" : NewBodyOperationType.ADD, "depth" : 13 * mm, "offsetDistance" : 25 * mm});
        }
        {
            var Q0;
            Q0=makeQuery(id+"F29.opExtrude","CAP_FACE",FACE,{"disambiguationData":[OSD([sQuery(id+"F28.wireOp",EDGE,"E26.bottom"),sQuery(id+"F28.wireOp",EDGE,"E26.top"),sQuery(id+"F28.wireOp",EDGE,"E26.left"),sQuery(id+"F28.wireOp",EDGE,"E26.right")])],"isStart":false});
            var sketch = newSketch(context, id + "F30", { "sketchPlane" : qUnion([Q0])});
            skLineSegment(sketch, "E27.bottom", {"start": v(8.66, 18.53) * mm, "end": v(7.66, 18.53) * mm});
            skLineSegment(sketch, "E27.top", {"start": v(8.66, 12.53) * mm, "end": v(7.66, 12.53) * mm});
            skLineSegment(sketch, "E27.left", {"start": v(8.66, 18.53) * mm, "end": v(8.66, 12.53) * mm});
            skLineSegment(sketch, "E27.right", {"start": v(7.66, 18.53) * mm, "end": v(7.66, 12.53) * mm});
            skSolve(sketch);
        }
        {
            var Q0;
            Q0=makeQuery(id+"F30.imprint","IMPRINT",FACE,{"disambiguationData":[TD([[makeQuery(id+"F30.imprint","IMPRINT",EDGE,{"derivedFrom":sQuery(id+"F30.wireOp",EDGE,"E27.bottom")}),1.0]])]});
            extrude(context, id + "F31", {"entities" : qUnion([Q0]), "operationType" : NewBodyOperationType.REMOVE, "oppositeDirection" : true, "depth" : 6.5 * mm, "offsetDistance" : 25 * mm});
        }
        {
            var Q0;
            Q0=makeQuery(id+"F27.boolean.opBoolean","COPY",FACE,{"derivedFrom":makeQuery(id+"F27.opExtrude","CAP_FACE",FACE,{"disambiguationData":[OSD([sQuery(id+"F26.wireOp",EDGE,"E20"),sQuery(id+"F26.wireOp",EDGE,"E21"),sQuery(id+"F26.wireOp",EDGE,"E22"),sQuery(id+"F26.wireOp",EDGE,"E23"),sQuery(id+"F26.wireOp",EDGE,"E24"),sQuery(id+"F26.wireOp",EDGE,"E25")])],"isStart":false})});
            var sketch = newSketch(context, id + "F32", { "sketchPlane" : qUnion([Q0])});
            skLineSegment(sketch, "E28.bottom", {"start": v(-33.3, -2.5) * mm, "end": v(-31.65, -2.5) * mm});
            skLineSegment(sketch, "E28.top", {"start": v(-33.3, 0) * mm, "end": v(-31.65, 0) * mm});
            skLineSegment(sketch, "E28.left", {"start": v(-33.3, -2.5) * mm, "end": v(-33.3, 0) * mm});
            skLineSegment(sketch, "E28.right", {"start": v(-31.65, -2.5) * mm, "end": v(-31.65, 0) * mm});
            skSolve(sketch);
        }
        {
            var Q0;
            Q0 = qSketchRegion(id + "F32", true);
            extrude(context, id + "F33", {"entities" : qUnion([Q0]), "operationType" : NewBodyOperationType.REMOVE, "oppositeDirection" : true, "depth" : 1.5 * mm, "offsetDistance" : 25 * mm});
        }
        {
            var Q0;
            {var subQ2=sQuery(id+"F0.wireOp",EDGE,"E2.left");var subQ3=sQuery(id+"F0.wireOp",EDGE,"E2.bottom");var subQ6=sQuery(id+"F0.wireOp",EDGE,"E1.right");var subQ12=sQuery(id+"F0.wireOp",EDGE,"E0.right");var subQ14=sQuery(id+"F0.wireOp",EDGE,"E0.left");var subQ15=makeQuery(id+"F1.opExtrude","SWEPT_FACE",FACE,{"disambiguationData":[OSD([subQ14])]});var subQ20=sQuery(id+"F0.wireOp",EDGE,"E1.top");var subQ21=sQuery(id+"F0.wireOp",EDGE,"E4.bottom");var subQ22=sQuery(id+"F0.wireOp",EDGE,"E3.bottom");var subQ23=sQuery(id+"F0.wireOp",EDGE,"E0.bottom");var subQ26=sQuery(id+"F0.wireOp",EDGE,"E1.left");var subQ44=sQuery(id+"F9.wireOp",EDGE,"E8.top");var subQ45=sQuery(id+"F0.wireOp",EDGE,"E2.top");var subQ46=sQuery(id+"F0.wireOp",EDGE,"E0.top");var subQ48=makeQuery(id+"F1.opExtrude","SWEPT_FACE",FACE,{"disambiguationData":[OSD([subQ46])]});var subQ49=sQuery(id+"F0.wireOp",EDGE,"E2.right");var subQ50=sQuery(id+"F0.wireOp",EDGE,"E1.bottom");var subQ52=makeQuery(id+"F1.opExtrude","CAP_FACE",FACE,{"disambiguationData":[OSD([subQ23,subQ46,subQ14,subQ12,subQ50,subQ20,subQ26,subQ6,subQ3,subQ45,subQ2,subQ49,subQ22,subQ21])],"isStart":false});Q0=makeQuery(id+"F16.boolean.opBoolean","SPLIT",FACE,{"disambiguationData":[TD([subQ15])],"derivedFrom":makeQuery(id+"F14.boolean.opBoolean","SPLIT",FACE,{"disambiguationData":[TD([subQ48])],"derivedFrom":makeQuery(id+"F10.boolean.opBoolean","MERGE",FACE,{"derivedFrom":[subQ52,makeQuery(id+"F10.opExtrude","SWEPT_FACE",FACE,{"disambiguationData":[OSD([subQ44]),TDD([makeQuery(id+"F9.imprint","IMPRINT",EDGE,{"disambiguationData":[TD([[makeQuery(id+"F9.imprint","INTERSECT",VERTEX,{"derivedFrom":[makeQuery(id+"F1.opExtrude","SWEPT_EDGE",EDGE,{"disambiguationData":[OSD([subQ3,subQ2])]}),subQ44]}),1.0]])],"derivedFrom":subQ44})])]}),makeQuery(id+"F10.opExtrude","SWEPT_FACE",FACE,{"disambiguationData":[OSD([subQ44]),TDD([makeQuery(id+"F9.imprint","IMPRINT",EDGE,{"disambiguationData":[TD([[makeQuery(id+"F9.imprint","INTERSECT",VERTEX,{"derivedFrom":[makeQuery(id+"F1.opExtrude","SWEPT_EDGE",EDGE,{"disambiguationData":[OSD([subQ45,subQ2])]}),subQ44]}),-1.0]])],"derivedFrom":subQ44})])]})]})})});}
            var sketch = newSketch(context, id + "F34", { "sketchPlane" : qUnion([Q0])});
            skLineSegment(sketch, "E29.bottom", {"start": v(-39.29, 41.96) * mm, "end": v(8.66, 41.96) * mm});
            skLineSegment(sketch, "E29.top", {"start": v(-39.29, 44.96) * mm, "end": v(8.66, 44.96) * mm});
            skLineSegment(sketch, "E29.left", {"start": v(-39.29, 41.96) * mm, "end": v(-39.29, 44.96) * mm});
            skLineSegment(sketch, "E29.right", {"start": v(8.66, 41.96) * mm, "end": v(8.66, 44.96) * mm});
            skSolve(sketch);
        }
        {
            var Q0;
            {var subQ7=sQuery(id+"F34.wireOp",EDGE,"E29.top");Q0=makeQuery(id+"F34.imprint","IMPRINT",FACE,{"disambiguationData":[TD([[makeQuery(id+"F34.imprint","IMPRINT",EDGE,{"derivedFrom":subQ7}),-1.0]])]});}
            extrude(context, id + "F35", {"entities" : qUnion([Q0]), "operationType" : NewBodyOperationType.REMOVE, "oppositeDirection" : true, "depth" : 3.5 * mm, "offsetDistance" : 25 * mm});
        }
        {
            var Q0;
            {var subQ0=sQuery(id+"F0.wireOp",EDGE,"E4.bottom");var subQ1=sQuery(id+"F0.wireOp",EDGE,"E3.bottom");var subQ2=sQuery(id+"F0.wireOp",EDGE,"E0.bottom");Q0=makeQuery(id+"F2.boolean.opBoolean","MERGE",FACE,{"derivedFrom":[makeQuery(id+"F1.opExtrude","SWEPT_FACE",FACE,{"disambiguationData":[OSD([subQ2,subQ1,subQ0])]}),makeQuery(id+"F2.opExtrude","SWEPT_FACE",FACE,{"disambiguationData":[OSD([subQ2,subQ1,subQ0])]})]});}
            extrude(context, id + "F36", {"entities" : qUnion([Q0]), "operationType" : NewBodyOperationType.ADD, "depth" : 25 * mm, "offsetDistance" : 25 * mm});
        }
        {
            var Q0;
            {var subQ0=sQuery(id+"F0.wireOp",EDGE,"E4.bottom");var subQ1=sQuery(id+"F0.wireOp",EDGE,"E3.bottom");var subQ2=sQuery(id+"F0.wireOp",EDGE,"E0.bottom");var subQ4=sQuery(id+"F9.wireOp",EDGE,"E8.top");var subQ5=sQuery(id+"F0.wireOp",EDGE,"E2.left");var subQ6=sQuery(id+"F0.wireOp",EDGE,"E2.top");var subQ8=sQuery(id+"F0.wireOp",EDGE,"E0.top");var subQ10=makeQuery(id+"F1.opExtrude","SWEPT_FACE",FACE,{"disambiguationData":[OSD([subQ8])]});var subQ12=sQuery(id+"F0.wireOp",EDGE,"E2.right");var subQ13=sQuery(id+"F0.wireOp",EDGE,"E2.bottom");var subQ14=sQuery(id+"F0.wireOp",EDGE,"E1.right");var subQ15=sQuery(id+"F0.wireOp",EDGE,"E1.left");var subQ16=sQuery(id+"F0.wireOp",EDGE,"E1.top");var subQ17=sQuery(id+"F0.wireOp",EDGE,"E1.bottom");var subQ18=sQuery(id+"F0.wireOp",EDGE,"E0.right");var subQ19=sQuery(id+"F0.wireOp",EDGE,"E0.left");var subQ20=makeQuery(id+"F1.opExtrude","CAP_FACE",FACE,{"disambiguationData":[OSD([subQ2,subQ8,subQ19,subQ18,subQ17,subQ16,subQ15,subQ14,subQ13,subQ6,subQ5,subQ12,subQ1,subQ0])],"isStart":false});var subQ25=makeQuery(id+"F10.opExtrude","SWEPT_FACE",FACE,{"disambiguationData":[OSD([subQ4]),TDD([makeQuery(id+"F9.imprint","IMPRINT",EDGE,{"disambiguationData":[TD([[makeQuery(id+"F9.imprint","INTERSECT",VERTEX,{"derivedFrom":[makeQuery(id+"F1.opExtrude","SWEPT_EDGE",EDGE,{"disambiguationData":[OSD([subQ6,subQ5])]}),subQ4]}),-1.0]])],"derivedFrom":subQ4})])]});var subQ26=makeQuery(id+"F1.opExtrude","SWEPT_FACE",FACE,{"disambiguationData":[OSD([subQ18])]});var subQ30=makeQuery(id+"F10.opExtrude","SWEPT_FACE",FACE,{"disambiguationData":[OSD([subQ4]),TDD([makeQuery(id+"F9.imprint","IMPRINT",EDGE,{"disambiguationData":[TD([[makeQuery(id+"F9.imprint","INTERSECT",VERTEX,{"derivedFrom":[makeQuery(id+"F1.opExtrude","SWEPT_EDGE",EDGE,{"disambiguationData":[OSD([subQ13,subQ5])]}),subQ4]}),1.0]])],"derivedFrom":subQ4})])]});var subQ46=makeQuery(id+"F1.opExtrude","SWEPT_FACE",FACE,{"disambiguationData":[OSD([subQ19])]});Q0=makeQuery(id+"F36.boolean.opBoolean","MERGE",FACE,{"derivedFrom":[makeQuery(id+"FY4pRUuHJMejb4m_1.boolean.opBoolean","SPLIT",FACE,{"disambiguationData":[TD([subQ26])],"derivedFrom":makeQuery(id+"F35.boolean.opBoolean","SPLIT",FACE,{"disambiguationData":[TD([subQ46])],"derivedFrom":makeQuery(id+"F16.boolean.opBoolean","SPLIT",FACE,{"disambiguationData":[TD([subQ46])],"derivedFrom":makeQuery(id+"F14.boolean.opBoolean","SPLIT",FACE,{"disambiguationData":[TD([subQ10])],"derivedFrom":makeQuery(id+"F10.boolean.opBoolean","MERGE",FACE,{"derivedFrom":[subQ20,subQ30,subQ25]})})})})}),makeQuery(id+"F36.opExtrude","SWEPT_FACE",FACE,{"disambiguationData":[OSD([subQ2,subQ1,subQ0]),TDD([makeQuery(id+"FY4pRUuHJMejb4m_1.boolean.opBoolean","SPLIT",EDGE,{"disambiguationData":[TD([subQ26])],"derivedFrom":makeQuery(id+"F1.opExtrude","CAP_EDGE",EDGE,{"disambiguationData":[OSD([subQ2,subQ1,subQ0])],"isStart":false})})])]})]});}
            var sketch = newSketch(context, id + "F37", { "sketchPlane" : qUnion([Q0])});
            skLineSegment(sketch, "E30.bottom", {"start": v(8.66, 70.02) * mm, "end": v(-41.34, 70.02) * mm});
            skLineSegment(sketch, "E30.top", {"start": v(8.66, 60.02) * mm, "end": v(-41.34, 60.02) * mm});
            skLineSegment(sketch, "E30.left", {"start": v(8.66, 70.02) * mm, "end": v(8.66, 60.02) * mm});
            skLineSegment(sketch, "E30.right", {"start": v(-41.34, 70.02) * mm, "end": v(-41.34, 60.02) * mm});
            skSolve(sketch);
        }
        {
            var Q0;
            Q0 = qSketchRegion(id + "F37", true);
            extrude(context, id + "F38", {"entities" : qUnion([Q0]), "operationType" : NewBodyOperationType.REMOVE, "oppositeDirection" : true, "depth" : 15 * mm, "offsetDistance" : 25 * mm});
        }
        {
            var Q0;
            Q0=makeQuery(id+"F38.boolean.opBoolean","COPY",EDGE,{"derivedFrom":makeQuery(id+"F38.opExtrude","CAP_EDGE",EDGE,{"disambiguationData":[OSD([sQuery(id+"F37.wireOp",EDGE,"E30.left")])],"isStart":false})});
            var Q1;
            Q1=makeQuery(id+"F38.boolean.opBoolean","COPY",EDGE,{"derivedFrom":makeQuery(id+"F38.opExtrude","CAP_EDGE",EDGE,{"disambiguationData":[OSD([sQuery(id+"F37.wireOp",EDGE,"E30.right")])],"isStart":false})});
            fillet(context, id + "F39", {"entities" : qUnion([Q0, Q1]), "radius" : 5 * mm, "tangentPropagation" : true, "allowEdgeOverflow" : false});
        }
        {
            var Q0;
            {var subQ0=sQuery(id+"F0.wireOp",EDGE,"E4.bottom");var subQ1=sQuery(id+"F0.wireOp",EDGE,"E3.bottom");var subQ2=sQuery(id+"F0.wireOp",EDGE,"E0.bottom");var subQ4=sQuery(id+"F9.wireOp",EDGE,"E8.top");var subQ5=sQuery(id+"F0.wireOp",EDGE,"E2.left");var subQ6=sQuery(id+"F0.wireOp",EDGE,"E2.top");var subQ8=sQuery(id+"F0.wireOp",EDGE,"E0.top");var subQ10=makeQuery(id+"F1.opExtrude","SWEPT_FACE",FACE,{"disambiguationData":[OSD([subQ8])]});var subQ12=sQuery(id+"F0.wireOp",EDGE,"E2.right");var subQ13=sQuery(id+"F0.wireOp",EDGE,"E2.bottom");var subQ14=sQuery(id+"F0.wireOp",EDGE,"E1.right");var subQ15=sQuery(id+"F0.wireOp",EDGE,"E1.left");var subQ16=sQuery(id+"F0.wireOp",EDGE,"E1.top");var subQ17=sQuery(id+"F0.wireOp",EDGE,"E1.bottom");var subQ18=sQuery(id+"F0.wireOp",EDGE,"E0.right");var subQ19=sQuery(id+"F0.wireOp",EDGE,"E0.left");var subQ20=makeQuery(id+"F1.opExtrude","CAP_FACE",FACE,{"disambiguationData":[OSD([subQ2,subQ8,subQ19,subQ18,subQ17,subQ16,subQ15,subQ14,subQ13,subQ6,subQ5,subQ12,subQ1,subQ0])],"isStart":false});var subQ25=makeQuery(id+"F10.opExtrude","SWEPT_FACE",FACE,{"disambiguationData":[OSD([subQ4]),TDD([makeQuery(id+"F9.imprint","IMPRINT",EDGE,{"disambiguationData":[TD([[makeQuery(id+"F9.imprint","INTERSECT",VERTEX,{"derivedFrom":[makeQuery(id+"F1.opExtrude","SWEPT_EDGE",EDGE,{"disambiguationData":[OSD([subQ6,subQ5])]}),subQ4]}),-1.0]])],"derivedFrom":subQ4})])]});var subQ26=makeQuery(id+"F1.opExtrude","SWEPT_FACE",FACE,{"disambiguationData":[OSD([subQ18])]});var subQ30=makeQuery(id+"F10.opExtrude","SWEPT_FACE",FACE,{"disambiguationData":[OSD([subQ4]),TDD([makeQuery(id+"F9.imprint","IMPRINT",EDGE,{"disambiguationData":[TD([[makeQuery(id+"F9.imprint","INTERSECT",VERTEX,{"derivedFrom":[makeQuery(id+"F1.opExtrude","SWEPT_EDGE",EDGE,{"disambiguationData":[OSD([subQ13,subQ5])]}),subQ4]}),1.0]])],"derivedFrom":subQ4})])]});var subQ46=makeQuery(id+"F1.opExtrude","SWEPT_FACE",FACE,{"disambiguationData":[OSD([subQ19])]});Q0=makeQuery(id+"F36.boolean.opBoolean","MERGE",FACE,{"derivedFrom":[makeQuery(id+"FY4pRUuHJMejb4m_1.boolean.opBoolean","SPLIT",FACE,{"disambiguationData":[TD([subQ26])],"derivedFrom":makeQuery(id+"F35.boolean.opBoolean","SPLIT",FACE,{"disambiguationData":[TD([subQ46])],"derivedFrom":makeQuery(id+"F16.boolean.opBoolean","SPLIT",FACE,{"disambiguationData":[TD([subQ46])],"derivedFrom":makeQuery(id+"F14.boolean.opBoolean","SPLIT",FACE,{"disambiguationData":[TD([subQ10])],"derivedFrom":makeQuery(id+"F10.boolean.opBoolean","MERGE",FACE,{"derivedFrom":[subQ20,subQ30,subQ25]})})})})}),makeQuery(id+"F36.opExtrude","SWEPT_FACE",FACE,{"disambiguationData":[OSD([subQ2,subQ1,subQ0]),TDD([makeQuery(id+"FY4pRUuHJMejb4m_1.boolean.opBoolean","SPLIT",EDGE,{"disambiguationData":[TD([subQ26])],"derivedFrom":makeQuery(id+"F1.opExtrude","CAP_EDGE",EDGE,{"disambiguationData":[OSD([subQ2,subQ1,subQ0])],"isStart":false})})])]})]});}
            var sketch = newSketch(context, id + "F40", { "sketchPlane" : qUnion([Q0])});
            skLineSegment(sketch, "E31.bottom", {"start": v(-39.29, 44.96) * mm, "end": v(-36.29, 44.96) * mm});
            skLineSegment(sketch, "E31.top", {"start": v(-39.29, 60.02) * mm, "end": v(-36.29, 60.02) * mm});
            skLineSegment(sketch, "E31.left", {"start": v(-39.29, 44.96) * mm, "end": v(-39.29, 60.02) * mm});
            skLineSegment(sketch, "E31.right", {"start": v(-36.29, 44.96) * mm, "end": v(-36.29, 60.02) * mm});
            skLineSegment(sketch, "E32.bottom", {"start": v(-26.58, 57.27) * mm, "end": v(-36.29, 57.27) * mm});
            skLineSegment(sketch, "E32.top", {"start": v(-26.58, 47.53) * mm, "end": v(-36.29, 47.53) * mm});
            skLineSegment(sketch, "E32.left", {"start": v(-26.58, 57.27) * mm, "end": v(-26.58, 47.53) * mm});
            skLineSegment(sketch, "E32.right", {"start": v(-36.29, 57.27) * mm, "end": v(-36.29, 47.53) * mm});
            skLineSegment(sketch, "E33.bottom", {"start": v(8.66, 44.96) * mm, "end": v(5.66, 44.96) * mm});
            skLineSegment(sketch, "E33.top", {"start": v(8.66, 60.02) * mm, "end": v(5.66, 60.02) * mm});
            skLineSegment(sketch, "E33.left", {"start": v(8.66, 44.96) * mm, "end": v(8.66, 60.02) * mm});
            skLineSegment(sketch, "E33.right", {"start": v(5.66, 44.96) * mm, "end": v(5.66, 60.02) * mm});
            skSolve(sketch);
        }
        {
            var Q0;
            Q0=makeQuery(id+"F40.imprint","IMPRINT",FACE,{"disambiguationData":[TD([[makeQuery(id+"F40.imprint","IMPRINT",EDGE,{"derivedFrom":sQuery(id+"F40.wireOp",EDGE,"E32.bottom")}),1.0]])]});
            extrude(context, id + "F41", {"entities" : qUnion([Q0]), "operationType" : NewBodyOperationType.REMOVE, "oppositeDirection" : true, "depth" : 10 * mm, "offsetDistance" : 25 * mm});
        }
        {
            var Q0;
            {var subQ1=sQuery(id+"F40.wireOp",EDGE,"E31.bottom");Q0=makeQuery(id+"F40.imprint","IMPRINT",FACE,{"disambiguationData":[TD([[makeQuery(id+"F40.imprint","IMPRINT",EDGE,{"derivedFrom":subQ1}),1.0]])]});}
            extrude(context, id + "F42", {"entities" : qUnion([Q0]), "operationType" : NewBodyOperationType.REMOVE, "oppositeDirection" : true, "depth" : 3.5 * mm, "offsetDistance" : 25 * mm});
        }
        {
            var Q0;
            Q0=makeQuery(id+"F40.imprint","IMPRINT",FACE,{"disambiguationData":[TD([[makeQuery(id+"F40.imprint","IMPRINT",EDGE,{"derivedFrom":sQuery(id+"F40.wireOp",EDGE,"E33.bottom")}),1.0]])]});
            extrude(context, id + "F43", {"entities" : qUnion([Q0]), "operationType" : NewBodyOperationType.REMOVE, "oppositeDirection" : true, "depth" : 3.5 * mm, "offsetDistance" : 25 * mm});
        }
        {
            var Q0;
            Q0=makeQuery(id+"F1.opExtrude","SWEPT_FACE",FACE,{"disambiguationData":[OSD([sQuery(id+"F0.wireOp",EDGE,"E2.right")])]});
            var sketch = newSketch(context, id + "F44", { "sketchPlane" : qUnion([Q0])});
            skLineSegment(sketch, "E34.bottom", {"start": v(-24.54, 0) * mm, "end": v(35.46, 0) * mm});
            skLineSegment(sketch, "E34.top", {"start": v(-24.54, 3) * mm, "end": v(35.46, 3) * mm});
            skLineSegment(sketch, "E34.left", {"start": v(-24.54, 0) * mm, "end": v(-24.54, 3) * mm});
            skLineSegment(sketch, "E34.right", {"start": v(35.46, 0) * mm, "end": v(35.46, 3) * mm});
            skSolve(sketch);
        }
        {
            var Q0;
            Q0 = qSketchRegion(id + "F44", true);
            extrude(context, id + "F45", {"entities" : qUnion([Q0]), "operationType" : NewBodyOperationType.ADD, "depth" : 20 * mm, "offsetDistance" : 25 * mm});
        }
    });
